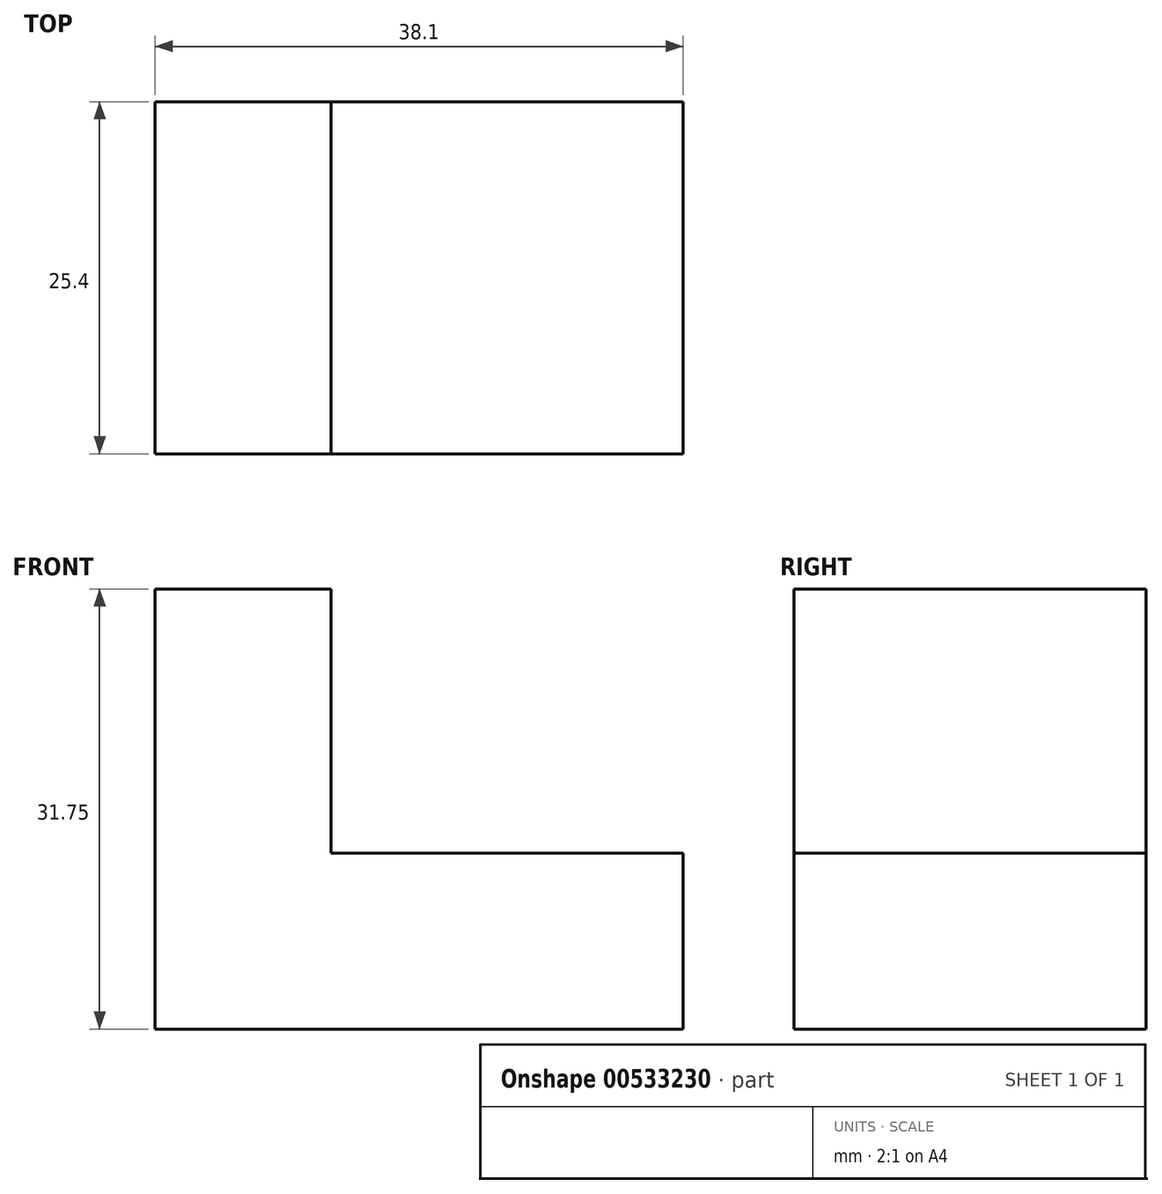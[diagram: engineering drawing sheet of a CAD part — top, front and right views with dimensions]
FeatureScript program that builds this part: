
annotation { "Feature Type Name" : "Feature", "Feature Type Description" : "" }
export const myFeature = defineFeature(function(context is Context, id is Id, definition is map)
    precondition{}
    {
        {
            var Q0;
            Q0=qCreatedBy(makeId("Front.planeOp"),FACE);
            var sketch = newSketch(context, id + "F0", { "sketchPlane" : qUnion([Q0])});
            skLineSegment(sketch, "E0", {"start": v(-56.45, 46.63) * mm, "end": v(-43.75, 46.63) * mm});
            skLineSegment(sketch, "E1", {"start": v(-56.45, 46.63) * mm, "end": v(-56.45, 14.88) * mm});
            skLineSegment(sketch, "E2", {"start": v(-43.75, 46.63) * mm, "end": v(-43.75, 27.58) * mm});
            skLineSegment(sketch, "E3", {"start": v(-43.75, 27.58) * mm, "end": v(-18.35, 27.58) * mm});
            skLineSegment(sketch, "E4", {"start": v(-56.45, 14.88) * mm, "end": v(-18.35, 14.88) * mm});
            skLineSegment(sketch, "E5", {"start": v(-18.35, 27.58) * mm, "end": v(-18.35, 14.88) * mm});
            skSolve(sketch);
        }
        {
            var Q0;
            Q0 = qSketchRegion(id + "F0", true);
            extrude(context, id + "F1", {"entities" : qUnion([Q0]), "depth" : 25.4 * mm, "offsetDistance" : 25.4 * mm});
        }
    });
